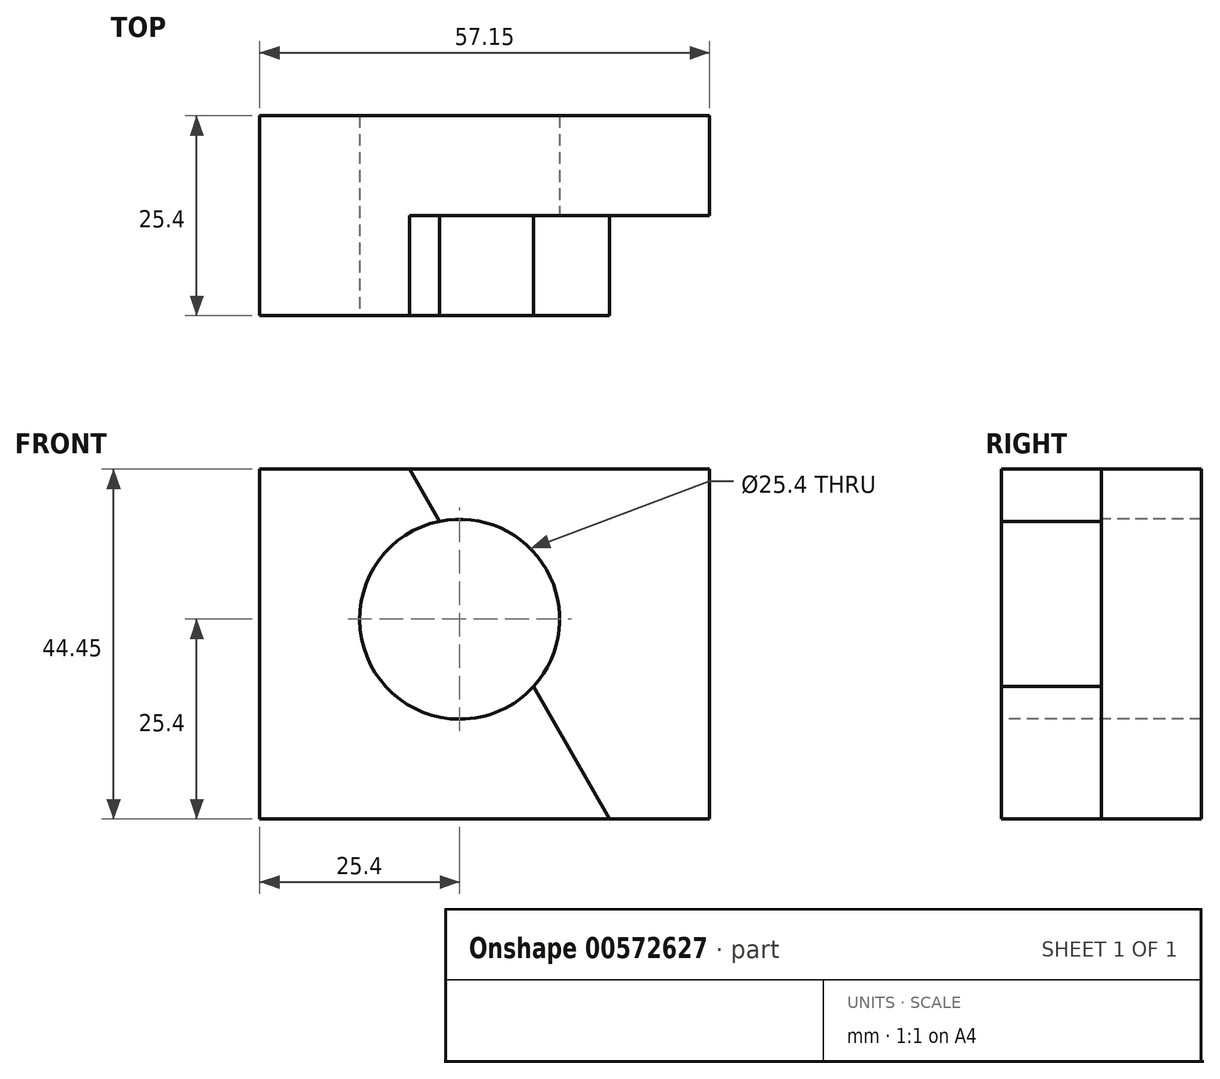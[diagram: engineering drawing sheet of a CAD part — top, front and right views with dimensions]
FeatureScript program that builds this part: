
annotation { "Feature Type Name" : "Feature", "Feature Type Description" : "" }
export const myFeature = defineFeature(function(context is Context, id is Id, definition is map)
    precondition{}
    {
        {
            var Q0;
            Q0=qCreatedBy(makeId("Front.planeOp"),FACE);
            var sketch = newSketch(context, id + "F0", { "sketchPlane" : qUnion([Q0])});
            skLineSegment(sketch, "E0", {"start": v(0, 0) * mm, "end": v(57.15, 0) * mm});
            skLineSegment(sketch, "E1", {"start": v(57.15, 0) * mm, "end": v(57.15, 44.45) * mm});
            skLineSegment(sketch, "E2", {"start": v(57.15, 44.45) * mm, "end": v(0, 44.45) * mm});
            skLineSegment(sketch, "E3", {"start": v(0, 44.45) * mm, "end": v(0, 0) * mm});
            skSolve(sketch);
        }
        {
            var Q0;
            Q0 = qSketchRegion(id + "F0", true);
            extrude(context, id + "F1", {"entities" : qUnion([Q0]), "depth" : 25.4 * mm, "offsetDistance" : 25.4 * mm});
        }
        {
            var Q0;
            Q0=makeQuery(id+"F1.opExtrude","CAP_FACE",FACE,{"disambiguationData":[OSD([sQuery(id+"F0.wireOp",EDGE,"E0"),sQuery(id+"F0.wireOp",EDGE,"E1"),sQuery(id+"F0.wireOp",EDGE,"E2"),sQuery(id+"F0.wireOp",EDGE,"E3")])],"isStart":false});
            var sketch = newSketch(context, id + "F2", { "sketchPlane" : qUnion([Q0])});
            skLineSegment(sketch, "E4", {"start": v(0, 44.45) * mm, "end": v(19.05, 44.45) * mm});
            skLineSegment(sketch, "E5", {"start": v(57.15, 0) * mm, "end": v(44.45, 0) * mm});
            skLineSegment(sketch, "E6", {"start": v(44.45, 0) * mm, "end": v(19.05, 44.45) * mm});
            skSolve(sketch);
        }
        {
            var Q0;
            Q0 = qSketchRegion(id + "F2", true);
            var Q1;
            Q1=makeQuery(id+"F2.imprint","IMPRINT",FACE,{"disambiguationData":[TD([[makeQuery(id+"F2.imprint","IMPRINT",EDGE,{"derivedFrom":sQuery(id+"F2.wireOp",EDGE,"E5")}),1.0]])]});
            extrude(context, id + "F3", {"entities" : qUnion([Q0, Q1]), "operationType" : NewBodyOperationType.REMOVE, "oppositeDirection" : true, "depth" : 12.7 * mm, "offsetDistance" : 25.4 * mm});
        }
        {
            var Q0;
            Q0=makeQuery(id+"F1.opExtrude","CAP_FACE",FACE,{"disambiguationData":[OSD([sQuery(id+"F0.wireOp",EDGE,"E0"),sQuery(id+"F0.wireOp",EDGE,"E1"),sQuery(id+"F0.wireOp",EDGE,"E2"),sQuery(id+"F0.wireOp",EDGE,"E3")])],"isStart":false});
            var sketch = newSketch(context, id + "F4", { "sketchPlane" : qUnion([Q0])});
            skCircle(sketch, "E7", {"center": v(25.4, 25.4) * mm, "radius": 12.7 * mm});
            skSolve(sketch);
        }
        {
            var Q0;
            Q0 = qSketchRegion(id + "F4", true);
            extrude(context, id + "F5", {"entities" : qUnion([Q0]), "operationType" : NewBodyOperationType.REMOVE, "oppositeDirection" : true, "depth" : 25.4 * mm, "offsetDistance" : 25.4 * mm});
        }
    });
